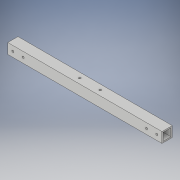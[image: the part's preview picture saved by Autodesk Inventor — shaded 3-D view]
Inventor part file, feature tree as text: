
AUTODESK INVENTOR PART (.ipt)
format: ipt  version: 2018 (Build 220112000, 112)  size: 135,680 bytes
history: native  units: in
note: dims shown in document units (in); Inventor stores cm internally (conversion verified against a paired STEP export)
features: extrude x3, sketch x3
ambient origin geometry x8: Origin, YZ Plane, XZ Plane, XY Plane, X Axis, Y Axis, Z Axis, Center Point
bodies: Solid1 (feature_tree)
feature tree (6):
  extrude  "Extrusion1"  Depth=1.0in
  extrude  "Extrusion2"  Depth=15.0in TaperAngle=0.0deg
  extrude  "Extrusion3"  Depth=1.0in
  sketch  "Sketch1"  dims[d0=1.0in d1=1.0in]
  sketch  "Sketch2"  dims[d2=0.125in d3=15.0in d4=0.0in]
  sketch  "Sketch3"  dims[d5=0.5in d6=1.0in d7=0.5in d8=1.0in d9=0.2031in d10=0.2031in d11=0.2031in d12=0.2031in d13=17.0in d14=0.0in d15=0.5in d16=90.0deg d17=1.0in d18=2.0in d19=0.2031in d20=3.0625in d21=0.0in]
